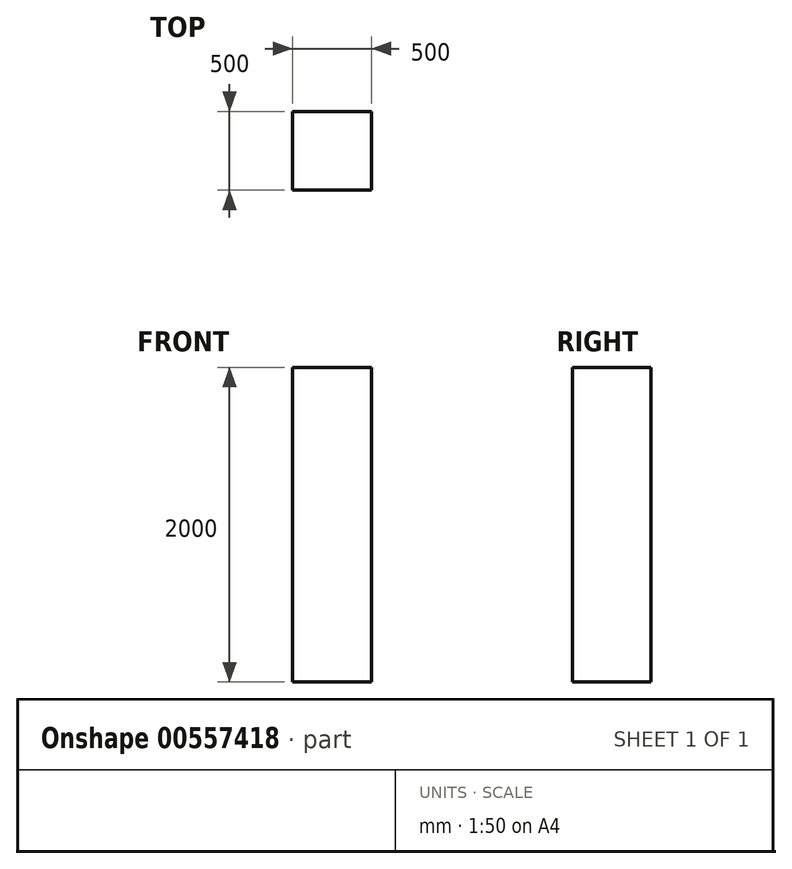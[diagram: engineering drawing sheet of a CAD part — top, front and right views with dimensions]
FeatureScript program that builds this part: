
annotation { "Feature Type Name" : "Feature", "Feature Type Description" : "" }
export const myFeature = defineFeature(function(context is Context, id is Id, definition is map)
    precondition{}
    {
        {
            var Q0;
            Q0=qCreatedBy(makeId("Front.planeOp"),FACE);
            var sketch = newSketch(context, id + "F0", { "sketchPlane" : qUnion([Q0])});
            skLineSegment(sketch, "E0.bottom", {"start": v(0, 0) * mm, "end": v(500, 0) * mm});
            skLineSegment(sketch, "E0.top", {"start": v(0, 2000) * mm, "end": v(500, 2000) * mm});
            skLineSegment(sketch, "E0.left", {"start": v(0, 0) * mm, "end": v(0, 2000) * mm});
            skLineSegment(sketch, "E0.right", {"start": v(500, 0) * mm, "end": v(500, 2000) * mm});
            skSolve(sketch);
        }
        {
            var Q0;
            Q0 = qSketchRegion(id + "F0", true);
            extrude(context, id + "F1", {"entities" : qUnion([Q0]), "depth" : 500 * mm, "offsetDistance" : 25 * mm});
        }
    });
